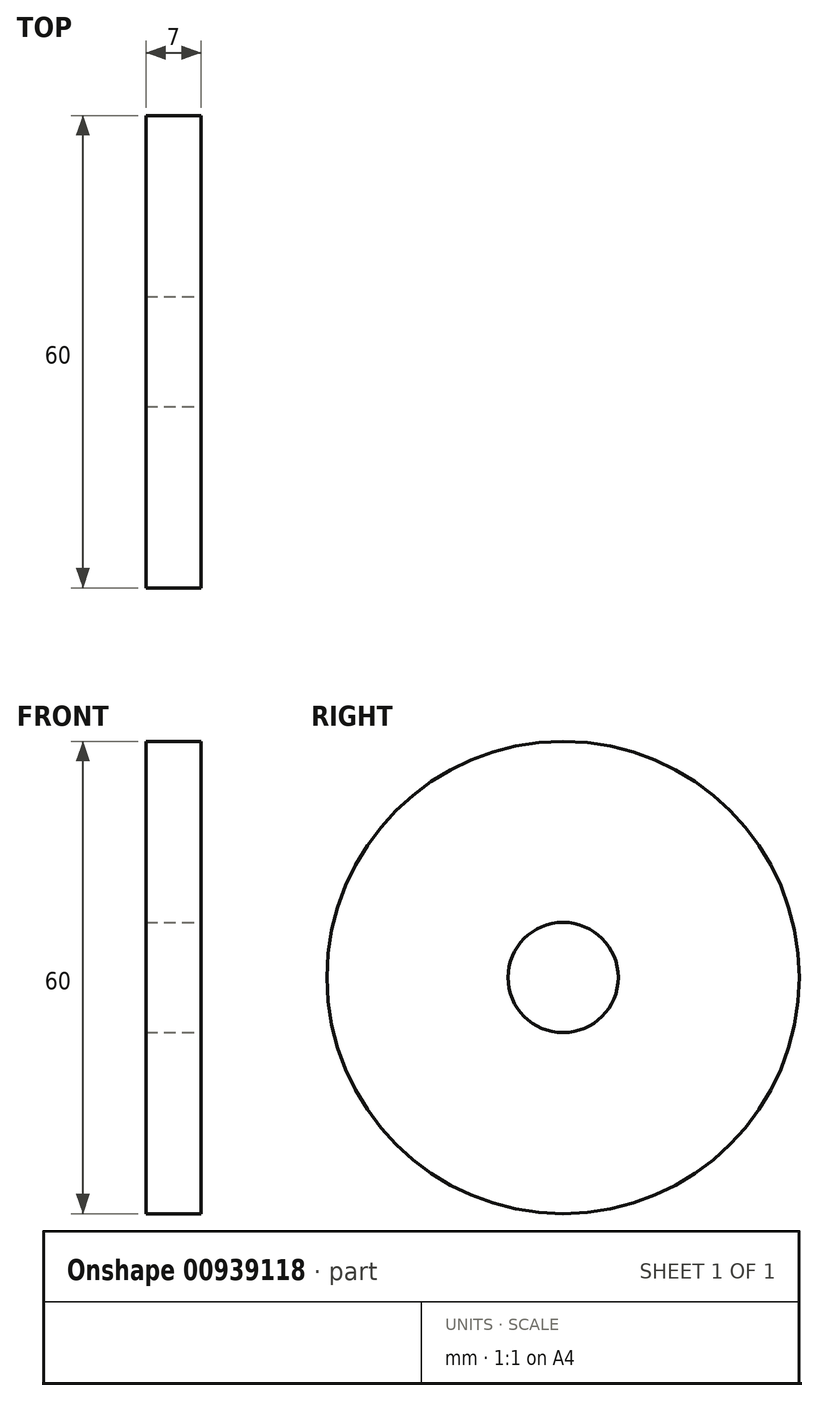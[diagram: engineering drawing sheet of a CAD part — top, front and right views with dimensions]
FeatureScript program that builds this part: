
annotation { "Feature Type Name" : "Feature", "Feature Type Description" : "" }
export const myFeature = defineFeature(function(context is Context, id is Id, definition is map)
    precondition{}
    {
        {
            var Q0;
            Q0=qCreatedBy(makeId("Right.planeOp"),FACE);
            var sketch = newSketch(context, id + "F0", { "sketchPlane" : qUnion([Q0])});
            skCircle(sketch, "E0", {"center": v(0, 0) * mm, "radius": 30 * mm});
            skSolve(sketch);
        }
        {
            var Q0;
            Q0=makeQuery(id+"F0.imprint","IMPRINT",FACE,{"disambiguationData":[TD([[makeQuery(id+"F0.imprint","IMPRINT",EDGE,{"derivedFrom":sQuery(id+"F0.wireOp",EDGE,"E0")}),1.0]])]});
            extrude(context, id + "F1", {"entities" : qUnion([Q0]), "depth" : 7 * mm, "offsetDistance" : 25 * mm});
        }
        {
            var Q0;
            Q0=qCreatedBy(makeId("Right.planeOp"),FACE);
            var sketch = newSketch(context, id + "F2", { "sketchPlane" : qUnion([Q0])});
            skCircle(sketch, "E1", {"center": v(0, 0) * mm, "radius": 7 * mm});
            skSolve(sketch);
        }
        {
            var Q0;
            Q0=makeQuery(id+"F2.imprint","IMPRINT",FACE,{"disambiguationData":[TD([[makeQuery(id+"F2.imprint","IMPRINT",EDGE,{"derivedFrom":sQuery(id+"F2.wireOp",EDGE,"E1")}),1.0]])]});
            extrude(context, id + "F3", {"entities" : qUnion([Q0]), "operationType" : NewBodyOperationType.REMOVE, "endBound" : BoundingType.SYMMETRIC, "oppositeDirection" : true, "depth" : 15 * mm, "offsetDistance" : 25 * mm});
        }
    });
